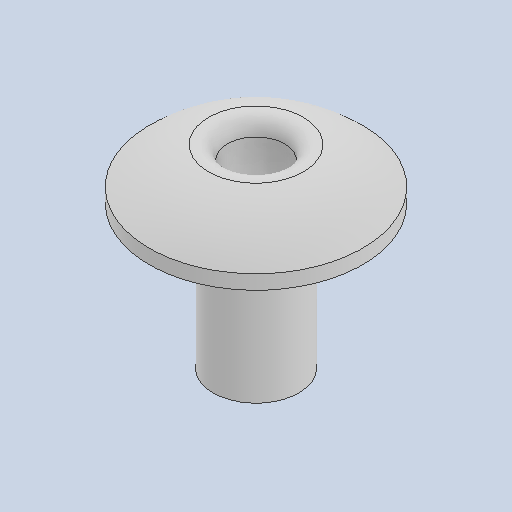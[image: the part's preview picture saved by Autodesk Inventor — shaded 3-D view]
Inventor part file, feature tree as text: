
AUTODESK INVENTOR PART (.ipt)
format: ipt  version: 2023 (Build 270158000, 158)  size: 103,424 bytes
history: native  units: mm
features: fillet x1
ambient origin geometry x8: Origin, YZ Plane, XZ Plane, XY Plane, X Axis, Y Axis, Z Axis, Center Point
bodies: Solid1 (feature_tree)
feature tree (1):
  fillet  "Fillet1"  [1 undecoded]
note: 1 required parameter value undecoded (feature->parameter linkage not recoverable at this tier; creation-order binding heuristic only, values carry confidence <= 0.55)
